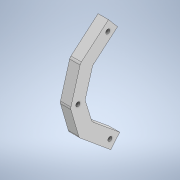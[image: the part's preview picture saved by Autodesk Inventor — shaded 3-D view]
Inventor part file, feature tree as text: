
AUTODESK INVENTOR PART (.ipt)
format: ipt  version: 2020 (Build 240168000, 168)  size: 166,400 bytes
history: native  units: in
note: dims shown in document units (in); Inventor stores cm internally (conversion verified against a paired STEP export)
features: extrude x2, sketch x2
ambient origin geometry x8: Origin, YZ Plane, XZ Plane, XY Plane, X Axis, Y Axis, Z Axis, Center Point
bodies: Solid1 (feature_tree)
feature tree (4):
  extrude  "Extrusion1"  Depth=0.3937in
  extrude  "Extrusion2"  Depth=0.2362in
  sketch  "Sketch2"  dims[d37=0.2362in d38=1.7717in d39=0.3937in d40=0.7874in d41=1.9685in d42=0.3937in d43=0.3937in d44=0.3937in d45=0.7874in d46=0.3937in d47=0.3937in d48=0.3937in d49=0.7874in d50=0.2362in d51=0.2362in d52=1.9685in d53=0.3937in d54=0.0069in d55=0.23in]
  sketch  "Sketch3"  dims[d56=0.4588in d57=0.6868in d58=2.9751in d59=3.0352in d60=0.8789in d61=2.9437in d62=1.661in d63=0.5906in d64=0.0in d65=0.2362in d66=0.3937in d67=0.3937in d68=0.2362in d69=0.3937in d70=0.3937in d71=0.2362in d72=0.0in d73=0.0in]
